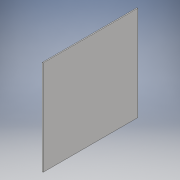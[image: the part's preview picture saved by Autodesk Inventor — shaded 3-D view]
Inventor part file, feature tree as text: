
AUTODESK INVENTOR PART (.ipt)
format: ipt  version: 2019 (Build 230136000, 136)  size: 89,088 bytes
history: native  units: mm
features: extrude x1, sketch x1
ambient origin geometry x8: Origin, YZ Plane, XZ Plane, XY Plane, X Axis, Y Axis, Z Axis, Center Point
bodies: Solid1 (feature_tree)
feature tree (2):
  extrude  "Extrusion1"  Depth=1000.0mm
  sketch  "Sketch1"  dims[d0=1000.0mm d1=1000.0mm d2=10.0mm d3=0.0mm]
